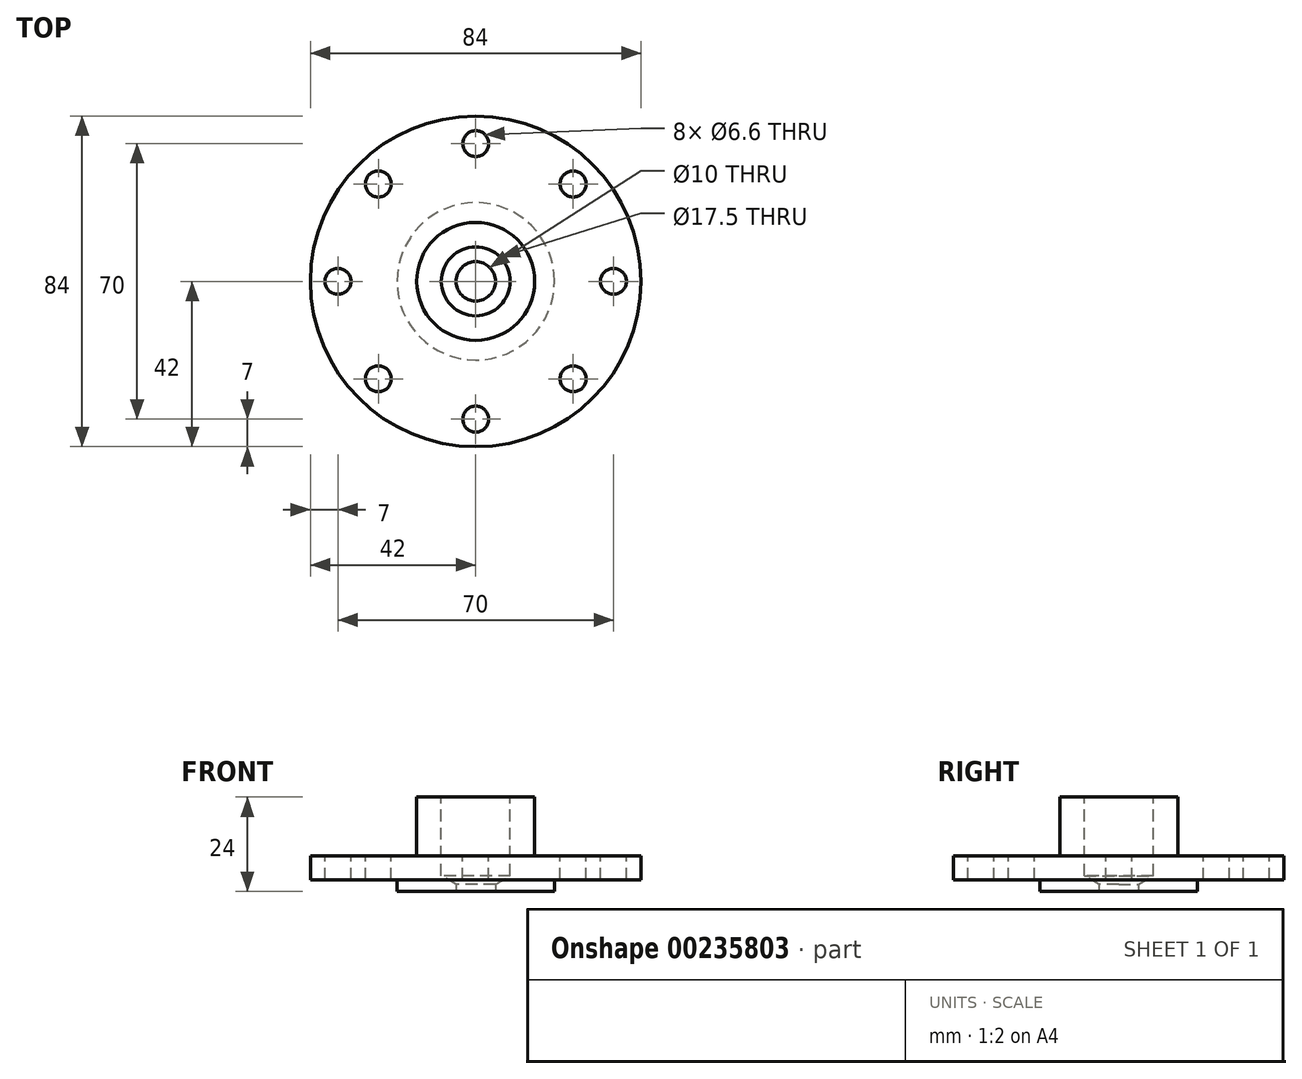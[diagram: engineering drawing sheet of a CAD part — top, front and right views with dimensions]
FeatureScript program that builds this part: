
annotation { "Feature Type Name" : "Feature", "Feature Type Description" : "" }
export const myFeature = defineFeature(function(context is Context, id is Id, definition is map)
    precondition{}
    {
        {
            var Q0;
            Q0=qCreatedBy(makeId("Top.planeOp"),FACE);
            var sketch = newSketch(context, id + "F0", { "sketchPlane" : qUnion([Q0])});
            skCircle(sketch, "E0", {"center": v(0, 0) * mm, "radius": 42 * mm});
            skSolve(sketch);
        }
        {
            var Q0;
            Q0=makeQuery(id+"F0.imprint","IMPRINT",FACE,{"disambiguationData":[TD([[makeQuery(id+"F0.imprint","IMPRINT",EDGE,{"derivedFrom":sQuery(id+"F0.wireOp",EDGE,"E0")}),1.0]])]});
            extrude(context, id + "F1", {"entities" : qUnion([Q0]), "depth" : 9 * mm});
        }
        {
            var Q0;
            Q0=makeQuery(id+"F1.opExtrude","CAP_FACE",FACE,{"disambiguationData":[OSD([sQuery(id+"F0.wireOp",EDGE,"E0")])],"isStart":true});
            var sketch = newSketch(context, id + "F2", { "sketchPlane" : qUnion([Q0])});
            skCircle(sketch, "E1", {"center": v(0, 0) * mm, "radius": 20 * mm});
            skSolve(sketch);
        }
        {
            var Q0;
            Q0=makeQuery(id+"F2.imprint","IMPRINT",FACE,{"disambiguationData":[TD([[makeQuery(id+"F2.imprint","IMPRINT",EDGE,{"derivedFrom":sQuery(id+"F2.wireOp",EDGE,"E1")}),-1.0]])]});
            extrude(context, id + "F3", {"entities" : qUnion([Q0]), "operationType" : NewBodyOperationType.REMOVE, "oppositeDirection" : true, "depth" : 3 * mm});
        }
        {
            var Q0;
            Q0=makeQuery(id+"F1.opExtrude","CAP_FACE",FACE,{"disambiguationData":[OSD([sQuery(id+"F0.wireOp",EDGE,"E0")])],"isStart":false});
            var sketch = newSketch(context, id + "F4", { "sketchPlane" : qUnion([Q0])});
            skCircle(sketch, "E2", {"center": v(0, 0) * mm, "radius": 15 * mm});
            skSolve(sketch);
        }
        {
            var Q0;
            Q0=makeQuery(id+"F4.imprint","IMPRINT",FACE,{"disambiguationData":[TD([[makeQuery(id+"F4.imprint","IMPRINT",EDGE,{"derivedFrom":sQuery(id+"F4.wireOp",EDGE,"E2")}),1.0]])]});
            extrude(context, id + "F5", {"entities" : qUnion([Q0]), "operationType" : NewBodyOperationType.ADD, "depth" : 15 * mm});
        }
        {
            var Q0;
            Q0=makeQuery(id+"F5.opExtrude","CAP_FACE",FACE,{"disambiguationData":[OSD([sQuery(id+"F4.wireOp",EDGE,"E2")])],"isStart":false});
            var sketch = newSketch(context, id + "F6", { "sketchPlane" : qUnion([Q0])});
            skPoint(sketch, "E3", {"position": v(0, 0) * mm});
            skSolve(sketch);
        }
        {
            var Q0;
            Q0=makeQuery(id+"F1.opExtrude","CAP_FACE",FACE,{"disambiguationData":[OSD([sQuery(id+"F0.wireOp",EDGE,"E0")])],"isStart":false});
            var sketch = newSketch(context, id + "F7", { "sketchPlane" : qUnion([Q0])});
            skCircle(sketch, "E4", {"center": v(0, 0) * mm, "radius": 35 * mm});
            skCircle(sketch, "E5", {"center": v(0, 35) * mm, "radius": 3.3 * mm});
            skCircle(sketch, "E6.1.0", {"center": v(-24.75, 24.75) * mm, "radius": 3.3 * mm});
            skCircle(sketch, "E6.2.0", {"center": v(-35, 0) * mm, "radius": 3.3 * mm});
            skCircle(sketch, "E6.3.0", {"center": v(-24.75, -24.75) * mm, "radius": 3.3 * mm});
            skCircle(sketch, "E6.4.0", {"center": v(0, -35) * mm, "radius": 3.3 * mm});
            skCircle(sketch, "E6.5.0", {"center": v(24.75, -24.75) * mm, "radius": 3.3 * mm});
            skCircle(sketch, "E6.6.0", {"center": v(35, 0) * mm, "radius": 3.3 * mm});
            skCircle(sketch, "E6.7.0", {"center": v(24.75, 24.75) * mm, "radius": 3.3 * mm});
            skSolve(sketch);
        }
        {
            var Q0;
            {var subQ0=sQuery(id+"F7.wireOp",EDGE,"E4");var subQ1=sQuery(id+"F7.wireOp",EDGE,"E5");var subQ2=makeQuery(id+"F7.imprint","INTERSECT",VERTEX,{"disambiguationData":[OD(0.0)],"derivedFrom":[subQ1,subQ0]});Q0=makeQuery(id+"F7.imprint","IMPRINT",FACE,{"disambiguationData":[TD([[makeQuery(id+"F7.imprint","IMPRINT",EDGE,{"disambiguationData":[TD([[subQ2,-1.0]])],"derivedFrom":subQ1}),1.0]])]});}
            var Q1;
            {var subQ0=sQuery(id+"F7.wireOp",EDGE,"E4");var subQ1=sQuery(id+"F7.wireOp",EDGE,"E5");var subQ2=makeQuery(id+"F7.imprint","INTERSECT",VERTEX,{"disambiguationData":[OD(0.0)],"derivedFrom":[subQ1,subQ0]});Q1=makeQuery(id+"F7.imprint","IMPRINT",FACE,{"disambiguationData":[TD([[makeQuery(id+"F7.imprint","IMPRINT",EDGE,{"disambiguationData":[TD([[subQ2,1.0]])],"derivedFrom":subQ1}),1.0]])]});}
            var Q2;
            {var subQ0=sQuery(id+"F7.wireOp",EDGE,"E4");var subQ1=sQuery(id+"F7.wireOp",EDGE,"E6.1.0");var subQ2=makeQuery(id+"F7.imprint","INTERSECT",VERTEX,{"disambiguationData":[OD(0.0)],"derivedFrom":[subQ1,subQ0]});Q2=makeQuery(id+"F7.imprint","IMPRINT",FACE,{"disambiguationData":[TD([[makeQuery(id+"F7.imprint","IMPRINT",EDGE,{"disambiguationData":[TD([[subQ2,1.0]])],"derivedFrom":subQ1}),1.0]])]});}
            var Q3;
            {var subQ0=sQuery(id+"F7.wireOp",EDGE,"E4");var subQ1=sQuery(id+"F7.wireOp",EDGE,"E6.1.0");var subQ2=makeQuery(id+"F7.imprint","INTERSECT",VERTEX,{"disambiguationData":[OD(0.0)],"derivedFrom":[subQ1,subQ0]});Q3=makeQuery(id+"F7.imprint","IMPRINT",FACE,{"disambiguationData":[TD([[makeQuery(id+"F7.imprint","IMPRINT",EDGE,{"disambiguationData":[TD([[subQ2,-1.0]])],"derivedFrom":subQ1}),1.0]])]});}
            var Q4;
            {var subQ0=sQuery(id+"F7.wireOp",EDGE,"E4");var subQ1=sQuery(id+"F7.wireOp",EDGE,"E6.2.0");var subQ2=makeQuery(id+"F7.imprint","INTERSECT",VERTEX,{"disambiguationData":[OD(0.0)],"derivedFrom":[subQ1,subQ0]});Q4=makeQuery(id+"F7.imprint","IMPRINT",FACE,{"disambiguationData":[TD([[makeQuery(id+"F7.imprint","IMPRINT",EDGE,{"disambiguationData":[TD([[subQ2,1.0]])],"derivedFrom":subQ1}),1.0]])]});}
            var Q5;
            {var subQ0=sQuery(id+"F7.wireOp",EDGE,"E4");var subQ1=sQuery(id+"F7.wireOp",EDGE,"E6.2.0");var subQ2=makeQuery(id+"F7.imprint","INTERSECT",VERTEX,{"disambiguationData":[OD(0.0)],"derivedFrom":[subQ1,subQ0]});Q5=makeQuery(id+"F7.imprint","IMPRINT",FACE,{"disambiguationData":[TD([[makeQuery(id+"F7.imprint","IMPRINT",EDGE,{"disambiguationData":[TD([[subQ2,-1.0]])],"derivedFrom":subQ1}),1.0]])]});}
            var Q6;
            {var subQ0=sQuery(id+"F7.wireOp",EDGE,"E4");var subQ1=sQuery(id+"F7.wireOp",EDGE,"E6.3.0");var subQ2=makeQuery(id+"F7.imprint","INTERSECT",VERTEX,{"disambiguationData":[OD(0.0)],"derivedFrom":[subQ1,subQ0]});Q6=makeQuery(id+"F7.imprint","IMPRINT",FACE,{"disambiguationData":[TD([[makeQuery(id+"F7.imprint","IMPRINT",EDGE,{"disambiguationData":[TD([[subQ2,-1.0]])],"derivedFrom":subQ1}),1.0]])]});}
            var Q7;
            {var subQ0=sQuery(id+"F7.wireOp",EDGE,"E4");var subQ1=sQuery(id+"F7.wireOp",EDGE,"E6.3.0");var subQ2=makeQuery(id+"F7.imprint","INTERSECT",VERTEX,{"disambiguationData":[OD(0.0)],"derivedFrom":[subQ1,subQ0]});Q7=makeQuery(id+"F7.imprint","IMPRINT",FACE,{"disambiguationData":[TD([[makeQuery(id+"F7.imprint","IMPRINT",EDGE,{"disambiguationData":[TD([[subQ2,1.0]])],"derivedFrom":subQ1}),1.0]])]});}
            var Q8;
            {var subQ0=sQuery(id+"F7.wireOp",EDGE,"E4");var subQ1=sQuery(id+"F7.wireOp",EDGE,"E6.4.0");var subQ2=makeQuery(id+"F7.imprint","INTERSECT",VERTEX,{"disambiguationData":[OD(0.0)],"derivedFrom":[subQ1,subQ0]});Q8=makeQuery(id+"F7.imprint","IMPRINT",FACE,{"disambiguationData":[TD([[makeQuery(id+"F7.imprint","IMPRINT",EDGE,{"disambiguationData":[TD([[subQ2,-1.0]])],"derivedFrom":subQ1}),1.0]])]});}
            var Q9;
            {var subQ0=sQuery(id+"F7.wireOp",EDGE,"E4");var subQ1=sQuery(id+"F7.wireOp",EDGE,"E6.4.0");var subQ2=makeQuery(id+"F7.imprint","INTERSECT",VERTEX,{"disambiguationData":[OD(0.0)],"derivedFrom":[subQ1,subQ0]});Q9=makeQuery(id+"F7.imprint","IMPRINT",FACE,{"disambiguationData":[TD([[makeQuery(id+"F7.imprint","IMPRINT",EDGE,{"disambiguationData":[TD([[subQ2,1.0]])],"derivedFrom":subQ1}),1.0]])]});}
            var Q10;
            {var subQ0=sQuery(id+"F7.wireOp",EDGE,"E4");var subQ1=sQuery(id+"F7.wireOp",EDGE,"E6.5.0");var subQ2=makeQuery(id+"F7.imprint","INTERSECT",VERTEX,{"disambiguationData":[OD(0.0)],"derivedFrom":[subQ1,subQ0]});Q10=makeQuery(id+"F7.imprint","IMPRINT",FACE,{"disambiguationData":[TD([[makeQuery(id+"F7.imprint","IMPRINT",EDGE,{"disambiguationData":[TD([[subQ2,1.0]])],"derivedFrom":subQ1}),1.0]])]});}
            var Q11;
            {var subQ0=sQuery(id+"F7.wireOp",EDGE,"E4");var subQ1=sQuery(id+"F7.wireOp",EDGE,"E6.5.0");var subQ2=makeQuery(id+"F7.imprint","INTERSECT",VERTEX,{"disambiguationData":[OD(0.0)],"derivedFrom":[subQ1,subQ0]});Q11=makeQuery(id+"F7.imprint","IMPRINT",FACE,{"disambiguationData":[TD([[makeQuery(id+"F7.imprint","IMPRINT",EDGE,{"disambiguationData":[TD([[subQ2,-1.0]])],"derivedFrom":subQ1}),1.0]])]});}
            var Q12;
            {var subQ0=sQuery(id+"F7.wireOp",EDGE,"E4");var subQ1=sQuery(id+"F7.wireOp",EDGE,"E6.6.0");var subQ2=makeQuery(id+"F7.imprint","INTERSECT",VERTEX,{"disambiguationData":[OD(0.0)],"derivedFrom":[subQ1,subQ0]});Q12=makeQuery(id+"F7.imprint","IMPRINT",FACE,{"disambiguationData":[TD([[makeQuery(id+"F7.imprint","IMPRINT",EDGE,{"disambiguationData":[TD([[subQ2,1.0]])],"derivedFrom":subQ1}),1.0]])]});}
            var Q13;
            {var subQ0=sQuery(id+"F7.wireOp",EDGE,"E4");var subQ1=sQuery(id+"F7.wireOp",EDGE,"E6.6.0");var subQ2=makeQuery(id+"F7.imprint","INTERSECT",VERTEX,{"disambiguationData":[OD(0.0)],"derivedFrom":[subQ1,subQ0]});Q13=makeQuery(id+"F7.imprint","IMPRINT",FACE,{"disambiguationData":[TD([[makeQuery(id+"F7.imprint","IMPRINT",EDGE,{"disambiguationData":[TD([[subQ2,-1.0]])],"derivedFrom":subQ1}),1.0]])]});}
            var Q14;
            {var subQ0=sQuery(id+"F7.wireOp",EDGE,"E4");var subQ1=sQuery(id+"F7.wireOp",EDGE,"E6.7.0");var subQ2=makeQuery(id+"F7.imprint","INTERSECT",VERTEX,{"disambiguationData":[OD(0.0)],"derivedFrom":[subQ1,subQ0]});Q14=makeQuery(id+"F7.imprint","IMPRINT",FACE,{"disambiguationData":[TD([[makeQuery(id+"F7.imprint","IMPRINT",EDGE,{"disambiguationData":[TD([[subQ2,-1.0]])],"derivedFrom":subQ1}),1.0]])]});}
            var Q15;
            {var subQ0=sQuery(id+"F7.wireOp",EDGE,"E4");var subQ1=sQuery(id+"F7.wireOp",EDGE,"E6.7.0");var subQ2=makeQuery(id+"F7.imprint","INTERSECT",VERTEX,{"disambiguationData":[OD(0.0)],"derivedFrom":[subQ1,subQ0]});Q15=makeQuery(id+"F7.imprint","IMPRINT",FACE,{"disambiguationData":[TD([[makeQuery(id+"F7.imprint","IMPRINT",EDGE,{"disambiguationData":[TD([[subQ2,1.0]])],"derivedFrom":subQ1}),1.0]])]});}
            extrude(context, id + "F8", {"entities" : qUnion([Q0, Q1, Q2, Q3, Q4, Q5, Q6, Q7, Q8, Q9, Q10, Q11, Q12, Q13, Q14, Q15]), "operationType" : NewBodyOperationType.REMOVE, "oppositeDirection" : true, "depth" : 25 * mm});
        }
        {
            var Q0;
            Q0=makeQuery(id+"F1.opExtrude","CAP_FACE",FACE,{"disambiguationData":[OSD([sQuery(id+"F0.wireOp",EDGE,"E0")])],"isStart":true});
            var sketch = newSketch(context, id + "F9", { "sketchPlane" : qUnion([Q0])});
            skCircle(sketch, "E7", {"center": v(0, 0) * mm, "radius": 5 * mm});
            skSolve(sketch);
        }
        {
            var Q0;
            Q0=makeQuery(id+"F9.imprint","IMPRINT",FACE,{"disambiguationData":[TD([[makeQuery(id+"F9.imprint","IMPRINT",EDGE,{"derivedFrom":sQuery(id+"F9.wireOp",EDGE,"E7")}),1.0]])]});
            extrude(context, id + "F10", {"entities" : qUnion([Q0]), "operationType" : NewBodyOperationType.REMOVE, "endBound" : BoundingType.THROUGH_ALL, "oppositeDirection" : true, "depth" : 25 * mm});
        }
        {
            var Q0;
            Q0=sQuery(id+"F6.wireOp",VERTEX,"E3");
            var Q1;
            Q1=makeQuery(id+"F1.opExtrude","SWEPT_BODY",BODY,{"disambiguationData":[OSD([sQuery(id+"F0.wireOp",EDGE,"E0")])]});
            hole(context, id + "F11", {"style" : HoleStyle.SIMPLE, "endStyle" : HoleEndStyle.BLIND, "holeDiameter" : 17.5 * mm, "holeDepth" : 20 * mm, "tappedDepth" : 12 * mm, "tapClearance" : 3, "startFromSketch" : true, "locations" : qUnion([Q0]), "scope" : qUnion([Q1])});
        }
    });
